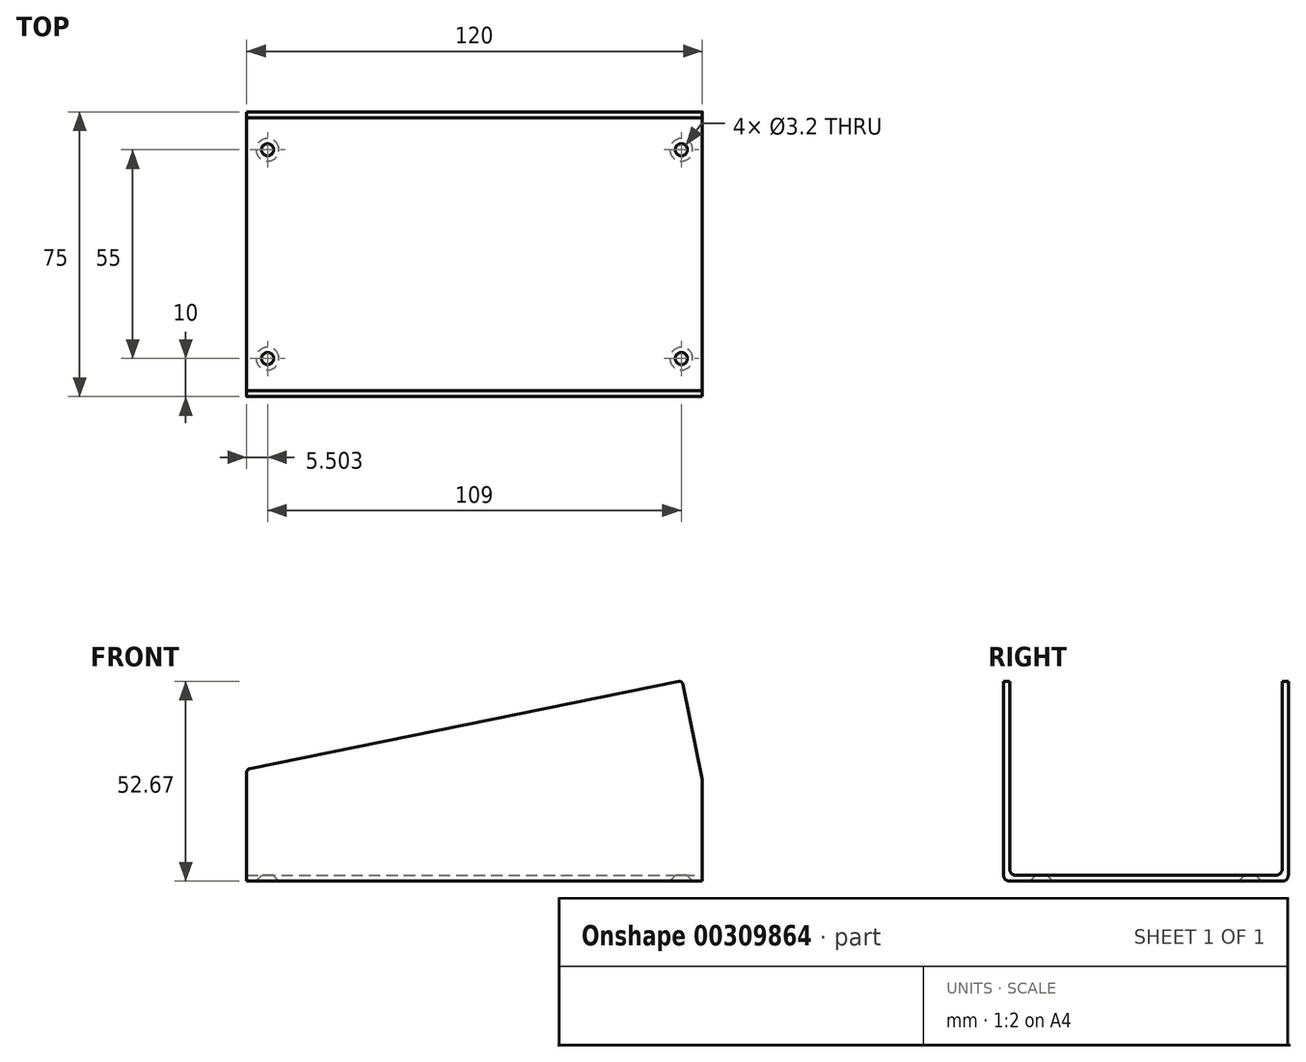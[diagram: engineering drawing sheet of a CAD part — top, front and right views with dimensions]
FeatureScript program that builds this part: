
annotation { "Feature Type Name" : "Feature", "Feature Type Description" : "" }
export const myFeature = defineFeature(function(context is Context, id is Id, definition is map)
    precondition{}
    {
        {
            var Q0;
            Q0=qCreatedBy(makeId("Front.planeOp"),FACE);
            var sketch = newSketch(context, id + "F0", { "sketchPlane" : qUnion([Q0])});
            skLineSegment(sketch, "E0", {"start": v(69.5, -20.81) * mm, "end": v(69.5, 6) * mm});
            skLineSegment(sketch, "E1", {"start": v(-50.5, 8.69) * mm, "end": v(64.2, 32.04) * mm});
            skLineSegment(sketch, "E2", {"start": v(-50.5, 8.69) * mm, "end": v(-50.5, -20.81) * mm});
            skLineSegment(sketch, "E3", {"start": v(-50.5, -20.81) * mm, "end": v(69.5, -20.81) * mm});
            skLineSegment(sketch, "E4", {"start": v(69.5, 6) * mm, "end": v(64.2, 32.04) * mm});
            skSolve(sketch);
        }
        {
            var Q0;
            Q0=makeQuery(id+"F0.imprint","IMPRINT",FACE,{"disambiguationData":[TD([[makeQuery(id+"F0.imprint","IMPRINT",EDGE,{"derivedFrom":sQuery(id+"F0.wireOp",EDGE,"E0")}),1.0]])]});
            extrude(context, id + "F1", {"entities" : qUnion([Q0]), "depth" : 75 * mm, "symmetric" : true});
        }
        {
            var Q0;
            Q0=makeQuery(id+"F1.opExtrude","SWEPT_FACE",FACE,{"disambiguationData":[OSD([sQuery(id+"F0.wireOp",EDGE,"l0t69VPQ-nK6x-9JQ1-x2O0-YxwOz6i0dntp")])]});
            var Q1;
            Q1=makeQuery(id+"F1.opExtrude","SWEPT_FACE",FACE,{"disambiguationData":[OSD([sQuery(id+"F0.wireOp",EDGE,"AEPDZd2A-MEGn-lmfu-d17e-fIoVPLaKwwLm")])]});
            var Q2;
            Q2=makeQuery(id+"F1.opExtrude","SWEPT_FACE",FACE,{"disambiguationData":[OSD([sQuery(id+"F0.wireOp",EDGE,"OBBsqcf7-oSRe-eFoy-5F4Z-EieY0a0dnqQp")])]});
            var Q3;
            Q3=makeQuery(id+"F1.opExtrude","SWEPT_FACE",FACE,{"disambiguationData":[OSD([sQuery(id+"F0.wireOp",EDGE,"E2")])]});
            var Q4;
            Q4=makeQuery(id+"F1.opExtrude","SWEPT_FACE",FACE,{"disambiguationData":[OSD([sQuery(id+"F0.wireOp",EDGE,"E1")])]});
            var Q5;
            Q5=makeQuery(id+"F1.opExtrude","SWEPT_FACE",FACE,{"disambiguationData":[OSD([sQuery(id+"F0.wireOp",EDGE,"E4")])]});
            var Q6;
            Q6=makeQuery(id+"F1.opExtrude","SWEPT_FACE",FACE,{"disambiguationData":[OSD([sQuery(id+"F0.wireOp",EDGE,"E0")])]});
            shell(context, id + "F2", {"entities" : qUnion([Q0, Q1, Q2, Q3, Q4, Q5, Q6]), "thickness" : 1.6 * mm});
        }
        {
            var Q0;
            {var subQ0=sQuery(id+"F0.wireOp",EDGE,"E3");Q0=makeQuery(id+"F2.opShell","OFFSET_EDGE",EDGE,{"disambiguationData":[OSD([subQ0]),TDD([makeQuery(id+"F1.opExtrude","CAP_EDGE",EDGE,{"disambiguationData":[OSD([subQ0])],"isStart":false})])]});}
            var Q1;
            {var subQ0=sQuery(id+"F0.wireOp",EDGE,"E3");Q1=makeQuery(id+"F2.opShell","OFFSET_EDGE",EDGE,{"disambiguationData":[OSD([subQ0]),TDD([makeQuery(id+"F1.opExtrude","CAP_EDGE",EDGE,{"disambiguationData":[OSD([subQ0])],"isStart":true})])]});}
            fillet(context, id + "F3", {"entities" : qUnion([Q0, Q1]), "radius" : 1.6 * mm, "tangentPropagation" : true, "allowEdgeOverflow" : false});
        }
        {
            var Q0;
            Q0=makeQuery(id+"F1.opExtrude","SWEPT_FACE",FACE,{"disambiguationData":[OSD([sQuery(id+"F0.wireOp",EDGE,"E3")])]});
            var sketch = newSketch(context, id + "F4", { "sketchPlane" : qUnion([Q0])});
            skPoint(sketch, "E5", {"position": v(64, 27.5) * mm});
            skPoint(sketch, "E6", {"position": v(64, -27.5) * mm});
            skPoint(sketch, "E7", {"position": v(-45, -27.5) * mm});
            skPoint(sketch, "E8", {"position": v(-45, 27.5) * mm});
            skSolve(sketch);
        }
        {
            var Q0;
            Q0=sQuery(id+"F4.wireOp",VERTEX,"E6");
            var Q1;
            Q1=sQuery(id+"F4.wireOp",VERTEX,"E7");
            var Q2;
            Q2=sQuery(id+"F4.wireOp",VERTEX,"E5");
            var Q3;
            Q3=sQuery(id+"F4.wireOp",VERTEX,"E8");
            var Q4;
            Q4=makeQuery(id+"F1.opExtrude","SWEPT_BODY",BODY,{"disambiguationData":[OSD([sQuery(id+"F0.wireOp",EDGE,"E0"),sQuery(id+"F0.wireOp",EDGE,"E1"),sQuery(id+"F0.wireOp",EDGE,"E2"),sQuery(id+"F0.wireOp",EDGE,"E3"),sQuery(id+"F0.wireOp",EDGE,"E4")])]});
            hole(context, id + "F5", {"style" : HoleStyle.C_SINK, "endStyle" : HoleEndStyle.THROUGH, "holeDiameter" : 3.2 * mm, "cSinkDiameter" : 6 * mm, "cSinkAngle" : 90 * degree, "tappedDepth" : 12 * mm, "tapClearance" : 3, "locations" : qUnion([Q0, Q1, Q2, Q3]), "scope" : qUnion([Q4]), "startStyle" : HoleStartStyle.SKETCH});
        }
        {
            var Q0;
            Q0=makeQuery(id+"F2.opShell","OFFSET_EDGE",EDGE,{"disambiguationData":[OSD([sQuery(id+"F0.wireOp",EDGE,"OBBsqcf7-oSRe-eFoy-5F4Z-EieY0a0dnqQp"),sQuery(id+"F0.wireOp",EDGE,"l0t69VPQ-nK6x-9JQ1-x2O0-YxwOz6i0dntp")])]});
            var Q1;
            Q1=makeQuery(id+"F1.opExtrude","SWEPT_EDGE",EDGE,{"disambiguationData":[OSD([sQuery(id+"F0.wireOp",EDGE,"OBBsqcf7-oSRe-eFoy-5F4Z-EieY0a0dnqQp"),sQuery(id+"F0.wireOp",EDGE,"l0t69VPQ-nK6x-9JQ1-x2O0-YxwOz6i0dntp")])]});
            var Q2;
            Q2=makeQuery(id+"F1.opExtrude","SWEPT_EDGE",EDGE,{"disambiguationData":[OSD([sQuery(id+"F0.wireOp",EDGE,"l0t69VPQ-nK6x-9JQ1-x2O0-YxwOz6i0dntp"),sQuery(id+"F0.wireOp",EDGE,"AEPDZd2A-MEGn-lmfu-d17e-fIoVPLaKwwLm")])]});
            var Q3;
            Q3=makeQuery(id+"F2.opShell","OFFSET_EDGE",EDGE,{"disambiguationData":[OSD([sQuery(id+"F0.wireOp",EDGE,"l0t69VPQ-nK6x-9JQ1-x2O0-YxwOz6i0dntp"),sQuery(id+"F0.wireOp",EDGE,"AEPDZd2A-MEGn-lmfu-d17e-fIoVPLaKwwLm")])]});
            var Q4;
            Q4=makeQuery(id+"F1.opExtrude","CAP_EDGE",EDGE,{"disambiguationData":[OSD([sQuery(id+"F0.wireOp",EDGE,"E3")])],"isStart":true});
            var Q5;
            Q5=makeQuery(id+"F1.opExtrude","CAP_EDGE",EDGE,{"disambiguationData":[OSD([sQuery(id+"F0.wireOp",EDGE,"E3")])],"isStart":false});
            fillet(context, id + "F6", {"entities" : qUnion([Q0, Q1, Q2, Q3, Q4, Q5]), "radius" : 1.6 * mm, "tangentPropagation" : true, "allowEdgeOverflow" : false});
        }
        {
            var Q0;
            Q0=makeQuery(id+"F2.opShell","OFFSET_EDGE",EDGE,{"disambiguationData":[OSD([sQuery(id+"F0.wireOp",EDGE,"E1"),sQuery(id+"F0.wireOp",EDGE,"E4")])]});
            var Q1;
            Q1=makeQuery(id+"F1.opExtrude","SWEPT_EDGE",EDGE,{"disambiguationData":[OSD([sQuery(id+"F0.wireOp",EDGE,"E1"),sQuery(id+"F0.wireOp",EDGE,"E4")])]});
            var Q2;
            Q2=makeQuery(id+"F1.opExtrude","SWEPT_EDGE",EDGE,{"disambiguationData":[OSD([sQuery(id+"F0.wireOp",EDGE,"E0"),sQuery(id+"F0.wireOp",EDGE,"E4")])]});
            var Q3;
            Q3=makeQuery(id+"F2.opShell","OFFSET_EDGE",EDGE,{"disambiguationData":[OSD([sQuery(id+"F0.wireOp",EDGE,"E0"),sQuery(id+"F0.wireOp",EDGE,"E4")])]});
            var Q4;
            Q4=makeQuery(id+"F2.opShell","OFFSET_EDGE",EDGE,{"disambiguationData":[OSD([sQuery(id+"F0.wireOp",EDGE,"E1"),sQuery(id+"F0.wireOp",EDGE,"E2")])]});
            var Q5;
            Q5=makeQuery(id+"F1.opExtrude","SWEPT_EDGE",EDGE,{"disambiguationData":[OSD([sQuery(id+"F0.wireOp",EDGE,"E1"),sQuery(id+"F0.wireOp",EDGE,"E2")])]});
            fillet(context, id + "F7", {"entities" : qUnion([Q0, Q1, Q2, Q3, Q4, Q5]), "radius" : 1 * mm, "tangentPropagation" : true, "allowEdgeOverflow" : false});
        }
    });
